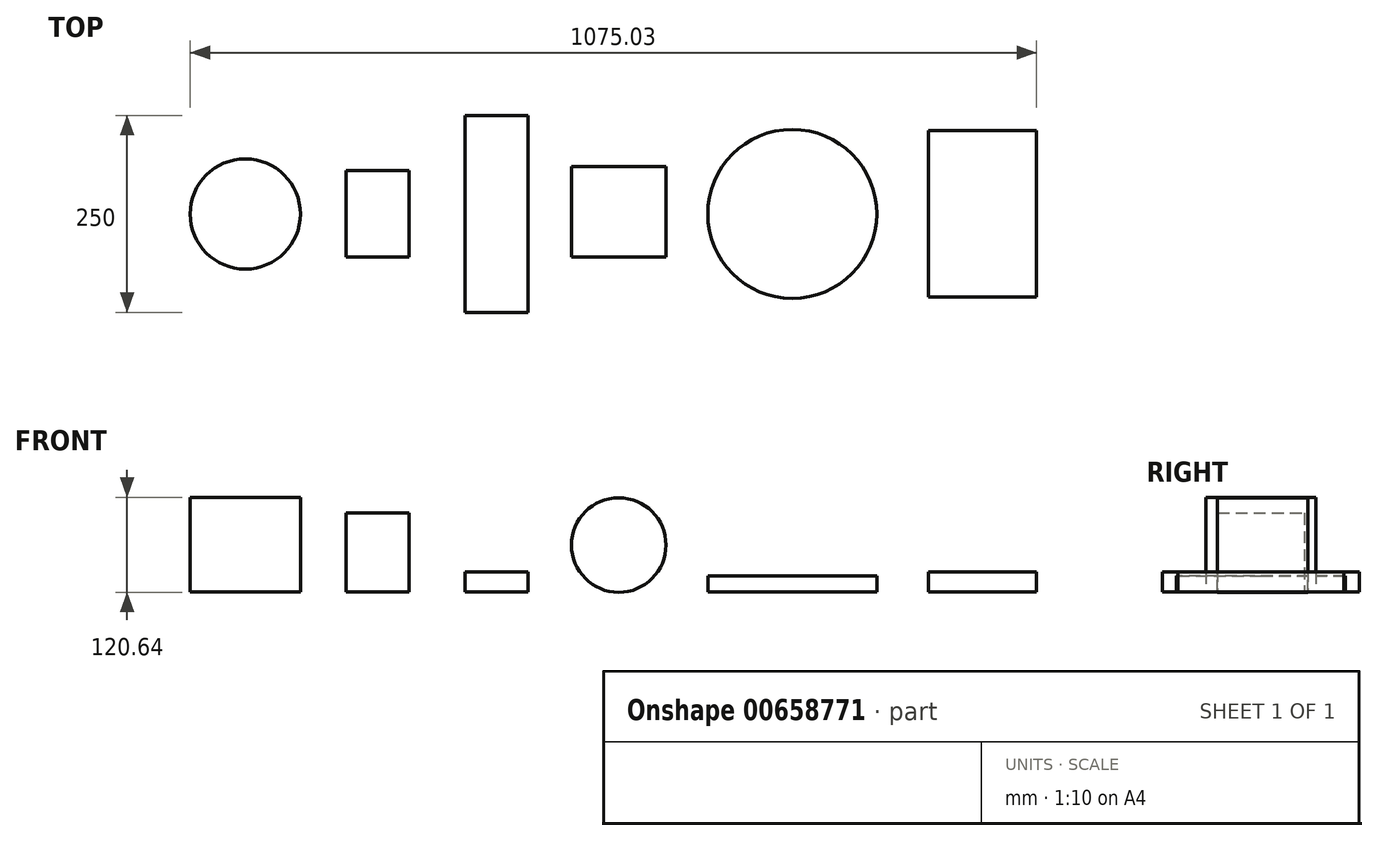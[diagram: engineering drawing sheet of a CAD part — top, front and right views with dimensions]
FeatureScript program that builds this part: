
annotation { "Feature Type Name" : "Feature", "Feature Type Description" : "" }
export const myFeature = defineFeature(function(context is Context, id is Id, definition is map)
    precondition{}
    {
        {
            var Q0;
            Q0=qCreatedBy(makeId("Top.planeOp"),FACE);
            var sketch = newSketch(context, id + "F0", { "sketchPlane" : qUnion([Q0])});
            skCircle(sketch, "E0", {"center": v(-109, 0) * mm, "radius": 70 * mm});
            skSolve(sketch);
        }
        {
            var Q0;
            Q0 = qSketchRegion(id + "F0", true);
            extrude(context, id + "F1", {"entities" : qUnion([Q0]), "depth" : 120 * mm, "offsetDistance" : 25 * mm});
        }
        {
            var Q0;
            Q0=qCreatedBy(makeId("Top.planeOp"),FACE);
            var sketch = newSketch(context, id + "F2", { "sketchPlane" : qUnion([Q0])});
            skLineSegment(sketch, "E1.bottom", {"start": v(99.05, -55) * mm, "end": v(19.05, -55) * mm});
            skLineSegment(sketch, "E1.top", {"start": v(99.05, 55) * mm, "end": v(19.05, 55) * mm});
            skLineSegment(sketch, "E1.left", {"start": v(99.05, -55) * mm, "end": v(99.05, 55) * mm});
            skLineSegment(sketch, "E1.right", {"start": v(19.05, -55) * mm, "end": v(19.05, 55) * mm});
            skPoint(sketch, "E1.middle", {"position": v(59.05, 0) * mm});
            skSolve(sketch);
        }
        {
            var Q0;
            Q0 = qSketchRegion(id + "F2", true);
            extrude(context, id + "F3", {"entities" : qUnion([Q0]), "depth" : 100 * mm, "offsetDistance" : 25 * mm});
        }
        {
            var Q0;
            Q0=qCreatedBy(makeId("Top.planeOp"),FACE);
            var sketch = newSketch(context, id + "F4", { "sketchPlane" : qUnion([Q0])});
            skLineSegment(sketch, "E2.bottom", {"start": v(169.93, -125) * mm, "end": v(249.93, -125) * mm});
            skLineSegment(sketch, "E2.top", {"start": v(169.93, 125) * mm, "end": v(249.93, 125) * mm});
            skLineSegment(sketch, "E2.left", {"start": v(169.93, -125) * mm, "end": v(169.93, 125) * mm});
            skLineSegment(sketch, "E2.right", {"start": v(249.93, -125) * mm, "end": v(249.93, 125) * mm});
            skPoint(sketch, "E2.middle", {"position": v(209.93, 0) * mm});
            skSolve(sketch);
        }
        {
            var Q0;
            Q0 = qSketchRegion(id + "F4", true);
            extrude(context, id + "F5", {"entities" : qUnion([Q0]), "depth" : 25 * mm, "offsetDistance" : 25 * mm});
        }
        {
            var Q0;
            Q0=qCreatedBy(makeId("Front.planeOp"),FACE);
            var sketch = newSketch(context, id + "F6", { "sketchPlane" : qUnion([Q0])});
            skCircle(sketch, "E3", {"center": v(365.38, 59.36) * mm, "radius": 60 * mm});
            skSolve(sketch);
        }
        {
            var Q0;
            Q0 = qSketchRegion(id + "F6", true);
            extrude(context, id + "F7", {"entities" : qUnion([Q0]), "depth" : 55 * mm, "offsetDistance" : 25 * mm, "hasSecondDirection" : true, "secondDirectionOppositeDirection" : true, "secondDirectionDepth" : 60 * mm});
        }
        {
            var Q0;
            Q0=qCreatedBy(makeId("Top.planeOp"),FACE);
            var sketch = newSketch(context, id + "F8", { "sketchPlane" : qUnion([Q0])});
            skCircle(sketch, "E4", {"center": v(585.8, 0) * mm, "radius": 107.29 * mm});
            skSolve(sketch);
        }
        {
            var Q0;
            Q0 = qSketchRegion(id + "F8", true);
            extrude(context, id + "F9", {"entities" : qUnion([Q0]), "depth" : 20 * mm, "offsetDistance" : 25 * mm});
        }
        {
            var Q0;
            Q0=qCreatedBy(makeId("Top.planeOp"),FACE);
            var sketch = newSketch(context, id + "F10", { "sketchPlane" : qUnion([Q0])});
            skLineSegment(sketch, "E5.bottom", {"start": v(758.68, -105.7) * mm, "end": v(896.03, -105.7) * mm});
            skLineSegment(sketch, "E5.top", {"start": v(758.68, 105.7) * mm, "end": v(896.03, 105.7) * mm});
            skLineSegment(sketch, "E5.left", {"start": v(758.68, -105.7) * mm, "end": v(758.68, 105.7) * mm});
            skLineSegment(sketch, "E5.right", {"start": v(896.03, -105.7) * mm, "end": v(896.03, 105.7) * mm});
            skPoint(sketch, "E5.middle", {"position": v(827.36, 0) * mm});
            skSolve(sketch);
        }
        {
            var Q0;
            Q0 = qSketchRegion(id + "F10", true);
            extrude(context, id + "F11", {"entities" : qUnion([Q0]), "depth" : 25 * mm, "offsetDistance" : 25 * mm});
        }
    });
